annotation { "Feature Type Name" : "Feature", "Feature Type Description" : "" }
export const myFeature = defineFeature(function(context is Context, id is Id, definition is map)
    precondition{}
    {
        {
            var Q0;
            Q0=qCreatedBy(makeId("Front.planeOp"),FACE);
            var sketch = newSketch(context, id + "F0", { "sketchPlane" : qUnion([Q0])});
            skArc(sketch, "E0", {"start": v(0, 75) * mm, "mid": v(-53.03, 53.03) * mm, "end": v(-75, 0) * mm});
            skArc(sketch, "E1", {"start": v(-12.5, 0) * mm, "mid": v(-37.5, 25) * mm, "end": v(-62.5, 0) * mm});
            skArc(sketch, "E2", {"start": v(0, 15.6) * mm, "mid": v(24, 37.5) * mm, "end": v(0, 59.4) * mm});
            skLineSegment(sketch, "E3", {"start": v(0, 59.4) * mm, "end": v(0, 75) * mm});
            skLineSegment(sketch, "E4", {"start": v(0, 15.6) * mm, "end": v(0, 0) * mm});
            skLineSegment(sketch, "E5", {"start": v(0, 0) * mm, "end": v(-12.5, 0) * mm});
            skLineSegment(sketch, "E6", {"start": v(-62.5, 0) * mm, "end": v(-75, 0) * mm});
            skSolve(sketch);
        }
        {
            var Q0;
            Q0 = qSketchRegion(id + "F0", true);
            extrude(context, id + "F1", {"entities" : qUnion([Q0]), "depth" : 10 * mm});
        }
        {
            var Q0;
            Q0=qCreatedBy(makeId("Front.planeOp"),FACE);
            var sketch = newSketch(context, id + "F2", { "sketchPlane" : qUnion([Q0])});
            skArc(sketch, "E7.0", {"start": v(-68.74, 30) * mm, "mid": v(-73.42, 15.32) * mm, "end": v(-75, 0) * mm});
            skLineSegment(sketch, "E8", {"start": v(-75, 0) * mm, "end": v(-105, 0) * mm});
            skLineSegment(sketch, "E9", {"start": v(-105, 0) * mm, "end": v(-105, 30) * mm});
            skLineSegment(sketch, "E10", {"start": v(-105, 30) * mm, "end": v(-68.74, 30) * mm});
            skSolve(sketch);
        }
        {
            var Q0;
            Q0 = qSketchRegion(id + "F2", true);
            var Q1;
            Q1 = qSketchRegion(id + "F0", true);
            extrude(context, id + "F3", {"entities" : qUnion([Q0, Q1]), "depth" : 10 * mm});
        }
        {
            var Q0;
            Q0=makeQuery(id+"F1.opExtrude","SWEPT_BODY",BODY,{"disambiguationData":[OSD([sQuery(id+"F0.wireOp",EDGE,"E0"),sQuery(id+"F0.wireOp",EDGE,"E1"),sQuery(id+"F0.wireOp",EDGE,"E2"),sQuery(id+"F0.wireOp",EDGE,"E3"),sQuery(id+"F0.wireOp",EDGE,"E4"),sQuery(id+"F0.wireOp",EDGE,"E5"),sQuery(id+"F0.wireOp",EDGE,"E6")])]});
            transform(context, id + "F4", {"entities" : qUnion([Q0]), "transformType" : TransformType.TRANSLATION_3D, "dx" : 0 * mm, "dy" : 0 * mm, "dz" : 0 * mm, "makeCopy" : true});
        }
        {
            var Q0;
            Q0=qCreatedBy(makeId("Front.planeOp"),FACE);
            var sketch = newSketch(context, id + "F5", { "sketchPlane" : qUnion([Q0])});
            skArc(sketch, "E11.0", {"start": v(0, 75) * mm, "mid": v(-15.32, 73.42) * mm, "end": v(-30, 68.74) * mm});
            skLineSegment(sketch, "E12", {"start": v(0, 75) * mm, "end": v(0, 105) * mm});
            skLineSegment(sketch, "E13", {"start": v(0, 105) * mm, "end": v(-30, 105) * mm});
            skLineSegment(sketch, "E14", {"start": v(-30, 105) * mm, "end": v(-30, 68.74) * mm});
            skSolve(sketch);
        }
        {
            var Q0;
            Q0 = qSketchRegion(id + "F0", true);
            var Q1;
            Q1 = qSketchRegion(id + "F5", true);
            extrude(context, id + "F6", {"entities" : qUnion([Q0, Q1]), "depth" : 10 * mm});
        }
        {
            var Q0;
            Q0=makeQuery(id+"F6.opExtrude","SWEPT_BODY",BODY,{"disambiguationData":[OSD([sQuery(id+"F0.wireOp",EDGE,"E0"),sQuery(id+"F0.wireOp",EDGE,"E1"),sQuery(id+"F0.wireOp",EDGE,"E2"),sQuery(id+"F0.wireOp",EDGE,"E3"),sQuery(id+"F0.wireOp",EDGE,"E4"),sQuery(id+"F0.wireOp",EDGE,"E5"),sQuery(id+"F0.wireOp",EDGE,"E6")])]});
            var Q1;
            Q1=makeQuery(id+"F6.opExtrude","SWEPT_BODY",BODY,{"disambiguationData":[OSD([sQuery(id+"F5.wireOp",EDGE,"E11.0"),sQuery(id+"F5.wireOp",EDGE,"E12"),sQuery(id+"F5.wireOp",EDGE,"E13"),sQuery(id+"F5.wireOp",EDGE,"E14")])]});
            booleanBodies(context, id + "F7", {"operationType" : BooleanOperationType.UNION, "tools" : qUnion([Q0, Q1])});
        }
        {
            var Q0;
            Q0=qCreatedBy(makeId("Front.planeOp"),FACE);
            var sketch = newSketch(context, id + "F8", { "sketchPlane" : qUnion([Q0])});
            skLineSegment(sketch, "E15.0", {"start": v(-176.12, 48.74) * mm, "end": v(-176.12, 96.1) * mm});
            skLineSegment(sketch, "E15.1", {"start": v(-80.08, 41.32) * mm, "end": v(-176.12, 48.74) * mm});
            skLineSegment(sketch, "E15.2", {"start": v(-80.08, 45.64) * mm, "end": v(-80.08, 41.32) * mm});
            skLineSegment(sketch, "E15.3", {"start": v(-66.59, 35.16) * mm, "end": v(-80.08, 45.64) * mm});
            skLineSegment(sketch, "E15.4", {"start": v(-59.46, 46.72) * mm, "end": v(-66.59, 35.16) * mm});
            skLineSegment(sketch, "E15.5", {"start": v(-176.12, 96.1) * mm, "end": v(-80.08, 70.36) * mm});
            skLineSegment(sketch, "E15.6", {"start": v(-51.85, 48.14) * mm, "end": v(-59.46, 46.72) * mm});
            skLineSegment(sketch, "E15.7", {"start": v(-62.34, 68.54) * mm, "end": v(-40.53, 68.54) * mm});
            skLineSegment(sketch, "E15.8", {"start": v(-66.56, 67.28) * mm, "end": v(-62.34, 68.54) * mm});
            skLineSegment(sketch, "E15.9", {"start": v(-80.08, 67.28) * mm, "end": v(-66.56, 67.28) * mm});
            skLineSegment(sketch, "E15.10", {"start": v(-80.08, 70.36) * mm, "end": v(-80.08, 67.28) * mm});
            skLineSegment(sketch, "E15.11", {"start": v(-40.53, 68.54) * mm, "end": v(-37.13, 67.2) * mm});
            skLineSegment(sketch, "E15.12", {"start": v(-37.13, 67.2) * mm, "end": v(-26.99, 61.8) * mm});
            skLineSegment(sketch, "E15.13", {"start": v(-26.99, 61.8) * mm, "end": v(-19.03, 61.8) * mm});
            skArc(sketch, "E15.14", {"start": v(-20.15, 55.55) * mm, "mid": v(-17.34, 58.27) * mm, "end": v(-19.03, 61.8) * mm});
            skLineSegment(sketch, "E15.15", {"start": v(-20.15, 55.55) * mm, "end": v(-37.24, 55.55) * mm});
            skArc(sketch, "E15.16", {"start": v(-51.85, 48.14) * mm, "mid": v(-44.02, 50.8) * mm, "end": v(-37.24, 55.55) * mm});
            skSolve(sketch);
        }
        {
            var Q0;
            Q0 = qSketchRegion(id + "F8", true);
            extrude(context, id + "F9", {"entities" : qUnion([Q0]), "depth" : 15 * mm});
        }
        {
            var Q0;
            Q0=qCreatedBy(makeId("Front.planeOp"),FACE);
            var sketch = newSketch(context, id + "F10", { "sketchPlane" : qUnion([Q0])});
            skLineSegment(sketch, "E16.bottom", {"start": v(-30, 123.97) * mm, "end": v(32, 123.97) * mm});
            skLineSegment(sketch, "E16.top", {"start": v(-30, 113.97) * mm, "end": v(32, 113.97) * mm});
            skLineSegment(sketch, "E16.left", {"start": v(-30, 123.97) * mm, "end": v(-30, 113.97) * mm});
            skLineSegment(sketch, "E16.right", {"start": v(32, 123.97) * mm, "end": v(32, 113.97) * mm});
            skLineSegment(sketch, "E17.0", {"start": v(0, 105) * mm, "end": v(-30, 105) * mm});
            skLineSegment(sketch, "E18", {"start": v(-30, 105) * mm, "end": v(-30, 155.23) * mm});
            skLineSegment(sketch, "E19.bottom", {"start": v(-22.83, 145.75) * mm, "end": v(27.17, 145.75) * mm});
            skLineSegment(sketch, "E19.top", {"start": v(-22.83, 135.75) * mm, "end": v(27.17, 135.75) * mm});
            skLineSegment(sketch, "E19.left", {"start": v(-22.83, 145.75) * mm, "end": v(-22.83, 135.75) * mm});
            skLineSegment(sketch, "E19.right", {"start": v(27.17, 145.75) * mm, "end": v(27.17, 135.75) * mm});
            skLineSegment(sketch, "E20.bottom", {"start": v(-18.3, 162.92) * mm, "end": v(21.7, 162.92) * mm});
            skLineSegment(sketch, "E20.top", {"start": v(-18.3, 152.92) * mm, "end": v(21.7, 152.92) * mm});
            skLineSegment(sketch, "E20.left", {"start": v(-18.3, 162.92) * mm, "end": v(-18.3, 152.92) * mm});
            skLineSegment(sketch, "E20.right", {"start": v(21.7, 162.92) * mm, "end": v(21.7, 152.92) * mm});
            skSolve(sketch);
        }
        {
            var Q0;
            {var subQ0=sQuery(id+"F10.wireOp",EDGE,"E16.bottom");Q0=makeQuery(id+"F10.imprint","IMPRINT",FACE,{"disambiguationData":[TD([[makeQuery(id+"F10.imprint","IMPRINT",EDGE,{"derivedFrom":subQ0}),-1.0]])]});}
            extrude(context, id + "F11", {"entities" : qUnion([Q0]), "depth" : 10 * mm});
        }
        {
            var Q0;
            Q0=makeQuery(id+"F10.imprint","IMPRINT",FACE,{"disambiguationData":[TD([[makeQuery(id+"F10.imprint","IMPRINT",EDGE,{"derivedFrom":sQuery(id+"F10.wireOp",EDGE,"E19.bottom")}),-1.0]])]});
            extrude(context, id + "F12", {"entities" : qUnion([Q0]), "depth" : 10 * mm});
        }
        {
            var Q0;
            Q0=makeQuery(id+"F10.imprint","IMPRINT",FACE,{"disambiguationData":[TD([[makeQuery(id+"F10.imprint","IMPRINT",EDGE,{"derivedFrom":sQuery(id+"F10.wireOp",EDGE,"E20.bottom")}),-1.0]])]});
            extrude(context, id + "F13", {"entities" : qUnion([Q0]), "depth" : 10 * mm});
        }
        {
            var Q0;
            Q0=qCreatedBy(makeId("Front.planeOp"),FACE);
            var sketch = newSketch(context, id + "F14", { "sketchPlane" : qUnion([Q0])});
            skArc(sketch, "E21.0", {"start": v(-75.07, -17.96) * mm, "mid": v(-79.6, -25.62) * mm, "end": v(-77.11, -34.15) * mm});
            skLineSegment(sketch, "E21.1", {"start": v(-77.11, -34.15) * mm, "end": v(-77.11, -47.98) * mm});
            skArc(sketch, "E21.2", {"start": v(-77.11, -47.98) * mm, "mid": v(-83.83, -61.04) * mm, "end": v(-81.71, -75.57) * mm});
            skLineSegment(sketch, "E21.3", {"start": v(-81.71, -75.57) * mm, "end": v(-74.23, -90.9) * mm});
            skArc(sketch, "E21.4", {"start": v(-78.07, -107) * mm, "mid": v(-73.26, -99.64) * mm, "end": v(-74.23, -90.9) * mm});
            skArc(sketch, "E21.5", {"start": v(-75.07, -17.96) * mm, "mid": v(-68.42, -37.97) * mm, "end": v(-53.63, -53) * mm});
            skLineSegment(sketch, "E21.6", {"start": v(-79.17, -106.63) * mm, "end": v(-78.07, -107) * mm});
            skLineSegment(sketch, "E21.7", {"start": v(-79.17, -106.63) * mm, "end": v(-93.76, -164.56) * mm});
            skLineSegment(sketch, "E21.8", {"start": v(-93.76, -164.56) * mm, "end": v(-50.22, -164.56) * mm});
            skLineSegment(sketch, "E21.9", {"start": v(-50.22, -164.56) * mm, "end": v(-50.69, -116.42) * mm});
            skLineSegment(sketch, "E21.10", {"start": v(-52.6, -115.77) * mm, "end": v(-50.69, -116.42) * mm});
            skArc(sketch, "E21.11", {"start": v(-25.75, -33.37) * mm, "mid": v(-25.88, -32.5) * mm, "end": v(-26.15, -31.66) * mm});
            skArc(sketch, "E21.12", {"start": v(-26.15, -31.66) * mm, "mid": v(-34.64, -32.62) * mm, "end": v(-40.61, -38.72) * mm});
            skArc(sketch, "E21.13", {"start": v(-49.3, -53.18) * mm, "mid": v(-43.52, -46.81) * mm, "end": v(-40.61, -38.72) * mm});
            skLineSegment(sketch, "E21.14", {"start": v(-53.63, -53) * mm, "end": v(-49.3, -53.18) * mm});
            skArc(sketch, "E21.15", {"start": v(-25.75, -33.37) * mm, "mid": v(-30.56, -42.79) * mm, "end": v(-33.2, -53.03) * mm});
            skLineSegment(sketch, "E21.16", {"start": v(-33.2, -53.03) * mm, "end": v(-33.2, -61.68) * mm});
            skArc(sketch, "E21.17", {"start": v(-33.2, -61.68) * mm, "mid": v(-36.52, -67.28) * mm, "end": v(-37.68, -73.68) * mm});
            skArc(sketch, "E21.18", {"start": v(-48.74, -90.5) * mm, "mid": v(-41.7, -83.08) * mm, "end": v(-37.68, -73.68) * mm});
            skArc(sketch, "E21.19", {"start": v(-48.74, -90.5) * mm, "mid": v(-51.58, -94.03) * mm, "end": v(-52.6, -98.43) * mm});
            skLineSegment(sketch, "E21.20", {"start": v(-52.6, -98.43) * mm, "end": v(-52.6, -115.77) * mm});
            skSolve(sketch);
        }
        {
            var Q0;
            Q0 = qSketchRegion(id + "F14", true);
            extrude(context, id + "F15", {"entities" : qUnion([Q0]), "depth" : 15 * mm});
        }
        {
            var Q0;
            Q0=qCreatedBy(makeId("Front.planeOp"),FACE);
            var sketch = newSketch(context, id + "F16", { "sketchPlane" : qUnion([Q0])});
            skText(sketch, "E22", { "text": "Shared Responsibility", "fontName": "Arimo-Italic.ttf"});
            const initialGuessF16  = {"E22": [0, -0.24947, 1, 0, 0.0272]};
            skSetInitialGuess(sketch, initialGuessF16);
            skSolve(sketch);
        }
        {
            var Q0;
            Q0 = qSketchRegion(id + "F16", true);
            extrude(context, id + "F17", {"entities" : qUnion([Q0]), "operationType" : NewBodyOperationType.ADD, "depth" : 25 * mm});
        }
        {
            var Q0;
            Q0=qCreatedBy(makeId("Front.planeOp"),FACE);
            var sketch = newSketch(context, id + "F18", { "sketchPlane" : qUnion([Q0])});
            skLineSegment(sketch, "E23.bottom", {"start": v(1.59, -204.26) * mm, "end": v(123.59, -204.26) * mm});
            skLineSegment(sketch, "E23.top", {"start": v(1.59, -242.26) * mm, "end": v(123.59, -242.26) * mm});
            skLineSegment(sketch, "E23.left", {"start": v(-3.41, -209.26) * mm, "end": v(-3.41, -237.26) * mm});
            skLineSegment(sketch, "E23.right", {"start": v(128.59, -209.26) * mm, "end": v(128.59, -237.26) * mm});
            skPoint(sketch, "E24.visualSharp", {"position": v(-3.41, -204.26) * mm});
            skArc(sketch, "E24.filletArc", {"start": v(1.59, -204.26) * mm, "mid": v(-1.95, -205.73) * mm, "end": v(-3.41, -209.26) * mm});
            skPoint(sketch, "E25.visualSharp", {"position": v(128.59, -204.26) * mm});
            skArc(sketch, "E25.filletArc", {"start": v(128.59, -209.26) * mm, "mid": v(127.12, -205.73) * mm, "end": v(123.59, -204.26) * mm});
            skPoint(sketch, "E26.visualSharp", {"position": v(-3.41, -242.26) * mm});
            skArc(sketch, "E26.filletArc", {"start": v(-3.41, -237.26) * mm, "mid": v(-1.95, -240.8) * mm, "end": v(1.59, -242.26) * mm});
            skPoint(sketch, "E27.visualSharp", {"position": v(128.59, -242.26) * mm});
            skArc(sketch, "E27.filletArc", {"start": v(123.59, -242.26) * mm, "mid": v(127.12, -240.8) * mm, "end": v(128.59, -237.26) * mm});
            skArc(sketch, "E28.0", {"start": v(1.59, -203.26) * mm, "mid": v(-2.66, -205.02) * mm, "end": v(-4.41, -209.26) * mm});
            skLineSegment(sketch, "E28.1", {"start": v(-4.41, -209.26) * mm, "end": v(-4.41, -237.26) * mm});
            skLineSegment(sketch, "E28.2", {"start": v(1.59, -203.26) * mm, "end": v(123.59, -203.26) * mm});
            skArc(sketch, "E28.3", {"start": v(-4.41, -237.26) * mm, "mid": v(-2.66, -241.5) * mm, "end": v(1.59, -243.26) * mm});
            skArc(sketch, "E28.4", {"start": v(129.59, -209.26) * mm, "mid": v(127.83, -205.02) * mm, "end": v(123.59, -203.26) * mm});
            skLineSegment(sketch, "E28.5", {"start": v(129.59, -209.26) * mm, "end": v(129.59, -237.26) * mm});
            skArc(sketch, "E28.6", {"start": v(123.59, -243.26) * mm, "mid": v(127.83, -241.5) * mm, "end": v(129.59, -237.26) * mm});
            skLineSegment(sketch, "E28.7", {"start": v(1.59, -243.26) * mm, "end": v(123.59, -243.26) * mm});
            skSolve(sketch);
        }
        {
            var Q0;
            Q0 = qSketchRegion(id + "F18", true);
            extrude(context, id + "F19", {"entities" : qUnion([Q0]), "depth" : 25 * mm});
        }
        {
            var Q0;
            Q0=qCreatedBy(makeId("Front.planeOp"),FACE);
            var sketch = newSketch(context, id + "F20", { "sketchPlane" : qUnion([Q0])});
            skLineSegment(sketch, "E29.bottom", {"start": v(180, 170) * mm, "end": v(-180, 170) * mm});
            skLineSegment(sketch, "E29.top", {"start": v(180, -170) * mm, "end": v(-180, -170) * mm});
            skLineSegment(sketch, "E29.left", {"start": v(185, 165) * mm, "end": v(185, -165) * mm});
            skLineSegment(sketch, "E29.right", {"start": v(-185, 165) * mm, "end": v(-185, -165) * mm});
            skPoint(sketch, "E29.middle", {"position": v(0, 0) * mm});
            skPoint(sketch, "E30.visualSharp", {"position": v(-185, 170) * mm});
            skArc(sketch, "E30.filletArc", {"start": v(-180, 170) * mm, "mid": v(-183.54, 168.54) * mm, "end": v(-185, 165) * mm});
            skPoint(sketch, "E31.visualSharp", {"position": v(185, 170) * mm});
            skArc(sketch, "E31.filletArc", {"start": v(185, 165) * mm, "mid": v(183.54, 168.54) * mm, "end": v(180, 170) * mm});
            skPoint(sketch, "E32.visualSharp", {"position": v(185, -170) * mm});
            skArc(sketch, "E32.filletArc", {"start": v(180, -170) * mm, "mid": v(183.54, -168.54) * mm, "end": v(185, -165) * mm});
            skPoint(sketch, "E33.visualSharp", {"position": v(-185, -170) * mm});
            skArc(sketch, "E33.filletArc", {"start": v(-185, -165) * mm, "mid": v(-183.54, -168.54) * mm, "end": v(-180, -170) * mm});
            skArc(sketch, "E34.0", {"start": v(186, 165) * mm, "mid": v(184.24, 169.24) * mm, "end": v(180, 171) * mm});
            skLineSegment(sketch, "E34.1", {"start": v(186, 165) * mm, "end": v(186, -165) * mm});
            skLineSegment(sketch, "E34.2", {"start": v(180, 171) * mm, "end": v(-180, 171) * mm});
            skArc(sketch, "E34.3", {"start": v(180, -171) * mm, "mid": v(184.24, -169.24) * mm, "end": v(186, -165) * mm});
            skArc(sketch, "E34.4", {"start": v(-180, 171) * mm, "mid": v(-184.24, 169.24) * mm, "end": v(-186, 165) * mm});
            skLineSegment(sketch, "E34.5", {"start": v(-186, 165) * mm, "end": v(-186, -165) * mm});
            skArc(sketch, "E34.6", {"start": v(-186, -165) * mm, "mid": v(-184.24, -169.24) * mm, "end": v(-180, -171) * mm});
            skLineSegment(sketch, "E34.7", {"start": v(180, -171) * mm, "end": v(-180, -171) * mm});
            skSolve(sketch);
        }
        {
            var Q0;
            Q0 = qSketchRegion(id + "F20", true);
            extrude(context, id + "F21", {"entities" : qUnion([Q0]), "depth" : 25 * mm});
        }
        {
            var Q0;
            Q0=qCreatedBy(makeId("Front.planeOp"),FACE);
            var sketch = newSketch(context, id + "F22", { "sketchPlane" : qUnion([Q0])});
            skArc(sketch, "E35.0", {"start": v(-311.67, 99.03) * mm, "mid": v(-316.2, 91.37) * mm, "end": v(-313.71, 82.84) * mm});
            skLineSegment(sketch, "E35.1", {"start": v(-313.71, 82.84) * mm, "end": v(-313.71, 69.02) * mm});
            skArc(sketch, "E35.2", {"start": v(-313.71, 69.02) * mm, "mid": v(-320.43, 55.96) * mm, "end": v(-318.31, 41.43) * mm});
            skLineSegment(sketch, "E35.3", {"start": v(-318.31, 41.43) * mm, "end": v(-310.82, 26.1) * mm});
            skArc(sketch, "E35.4", {"start": v(-314.66, 9.98) * mm, "mid": v(-309.86, 17.35) * mm, "end": v(-310.82, 26.1) * mm});
            skArc(sketch, "E35.5", {"start": v(-311.67, 99.03) * mm, "mid": v(-305.01, 79.02) * mm, "end": v(-290.22, 64) * mm});
            skLineSegment(sketch, "E35.6", {"start": v(-315.76, 10.36) * mm, "end": v(-314.66, 9.98) * mm});
            skLineSegment(sketch, "E35.7", {"start": v(-315.76, 10.36) * mm, "end": v(-325.35, -27.67) * mm});
            skLineSegment(sketch, "E35.9", {"start": v(-287.02, -27.3) * mm, "end": v(-287.29, 0.57) * mm});
            skLineSegment(sketch, "E35.10", {"start": v(-289.19, 1.23) * mm, "end": v(-287.29, 0.57) * mm});
            skArc(sketch, "E35.11", {"start": v(-262.35, 83.62) * mm, "mid": v(-262.48, 84.5) * mm, "end": v(-262.75, 85.33) * mm});
            skArc(sketch, "E35.12", {"start": v(-262.75, 85.33) * mm, "mid": v(-271.24, 84.37) * mm, "end": v(-277.2, 78.27) * mm});
            skArc(sketch, "E35.13", {"start": v(-285.9, 63.81) * mm, "mid": v(-280.11, 70.18) * mm, "end": v(-277.2, 78.27) * mm});
            skLineSegment(sketch, "E35.14", {"start": v(-290.22, 64) * mm, "end": v(-285.9, 63.81) * mm});
            skArc(sketch, "E35.15", {"start": v(-262.35, 83.62) * mm, "mid": v(-267.15, 74.2) * mm, "end": v(-269.8, 63.96) * mm});
            skLineSegment(sketch, "E35.16", {"start": v(-269.8, 63.96) * mm, "end": v(-269.8, 55.31) * mm});
            skArc(sketch, "E35.17", {"start": v(-269.8, 55.31) * mm, "mid": v(-273.11, 49.72) * mm, "end": v(-274.27, 43.3) * mm});
            skArc(sketch, "E35.18", {"start": v(-285.34, 26.48) * mm, "mid": v(-278.3, 33.9) * mm, "end": v(-274.27, 43.3) * mm});
            skArc(sketch, "E35.19", {"start": v(-285.34, 26.48) * mm, "mid": v(-288.17, 22.96) * mm, "end": v(-289.19, 18.56) * mm});
            skLineSegment(sketch, "E35.20", {"start": v(-289.19, 18.56) * mm, "end": v(-289.19, 1.23) * mm});
            skLineSegment(sketch, "E36", {"start": v(-325.35, -27.67) * mm, "end": v(-287.02, -27.3) * mm});
            skPoint(sketch, "E36.endSnap0", {"position": v(-287.02, -27.3) * mm});
            skPoint(sketch, "E35.8.end.orphan", {"position": v(-286.75, -55.16) * mm});
            skSolve(sketch);
        }
        {
            var Q0;
            Q0 = qSketchRegion(id + "F22", true);
            extrude(context, id + "F23", {"entities" : qUnion([Q0]), "depth" : 25 * mm});
        }
    });